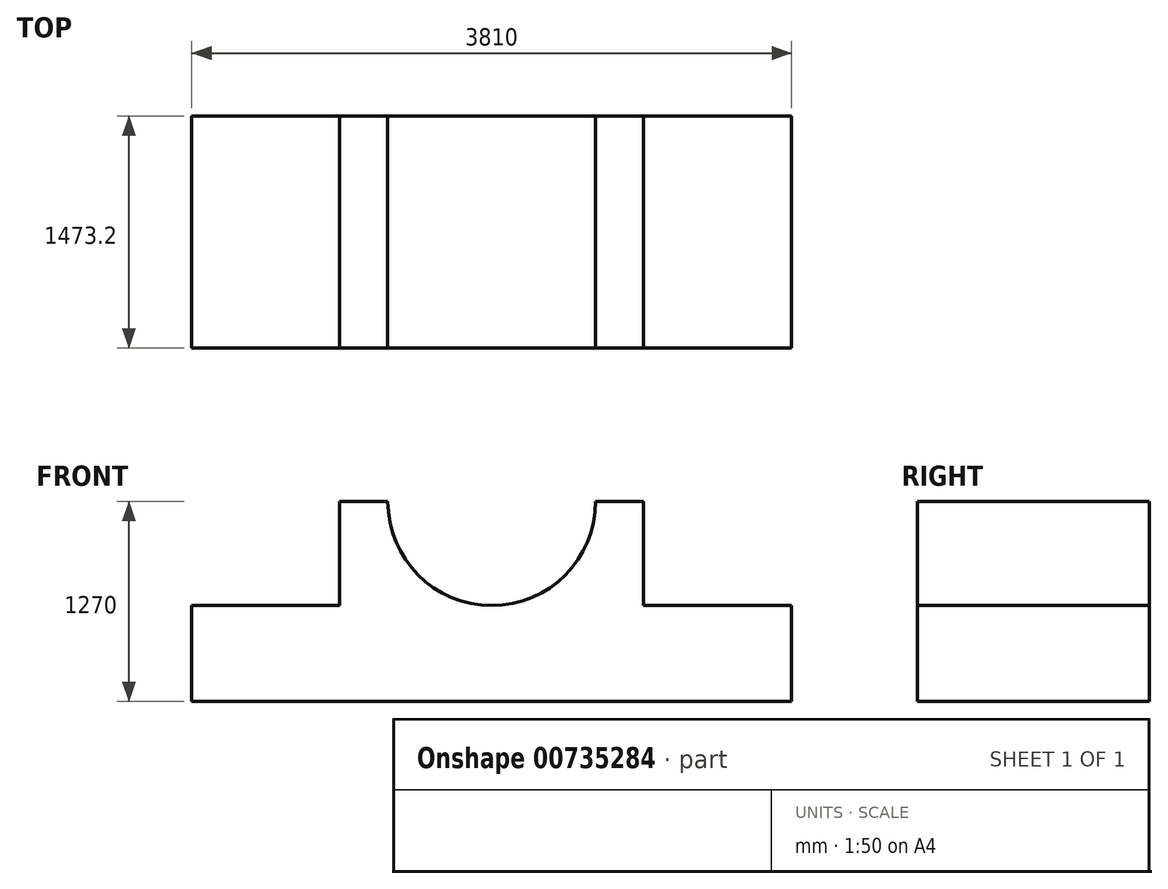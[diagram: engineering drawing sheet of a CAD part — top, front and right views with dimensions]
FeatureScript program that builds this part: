
annotation { "Feature Type Name" : "Feature", "Feature Type Description" : "" }
export const myFeature = defineFeature(function(context is Context, id is Id, definition is map)
    precondition{}
    {
        {
            var Q0;
            Q0=qCreatedBy(makeId("Front.planeOp"),FACE);
            var sketch = newSketch(context, id + "F0", { "sketchPlane" : qUnion([Q0])});
            skLineSegment(sketch, "E0", {"start": v(-66.4, -33.38) * mm, "end": v(3743.6, -33.38) * mm});
            skLineSegment(sketch, "E1", {"start": v(-66.4, -33.38) * mm, "end": v(-66.4, 576.22) * mm});
            skLineSegment(sketch, "E2", {"start": v(3743.6, -33.38) * mm, "end": v(3743.6, 576.22) * mm});
            skLineSegment(sketch, "E3", {"start": v(-66.4, 576.22) * mm, "end": v(873.4, 576.22) * mm});
            skLineSegment(sketch, "E4", {"start": v(3743.6, 576.22) * mm, "end": v(2803.8, 576.22) * mm});
            skLineSegment(sketch, "E5", {"start": v(2803.8, 576.22) * mm, "end": v(2803.8, 1236.62) * mm});
            skLineSegment(sketch, "E6", {"start": v(873.4, 576.22) * mm, "end": v(873.4, 1236.62) * mm});
            skLineSegment(sketch, "E7", {"start": v(873.4, 1236.62) * mm, "end": v(1178.2, 1236.62) * mm});
            skLineSegment(sketch, "E8", {"start": v(2803.8, 1236.62) * mm, "end": v(2499, 1236.62) * mm});
            skLineSegment(sketch, "E9", {"start": v(1178.2, 1236.62) * mm, "end": v(1838.6, 1236.62) * mm});
            skCircle(sketch, "E10", {"center": v(1838.6, 1236.62) * mm, "radius": 660.4 * mm});
            skSolve(sketch);
        }
        {
            var Q0;
            Q0=makeQuery(id+"F0.imprint","IMPRINT",FACE,{"disambiguationData":[TD([[makeQuery(id+"F0.imprint","IMPRINT",EDGE,{"derivedFrom":sQuery(id+"F0.wireOp",EDGE,"E0")}),1.0]])]});
            extrude(context, id + "F1", {"entities" : qUnion([Q0]), "depth" : 1473.2 * mm, "offsetDistance" : 25.4 * mm});
        }
    });
